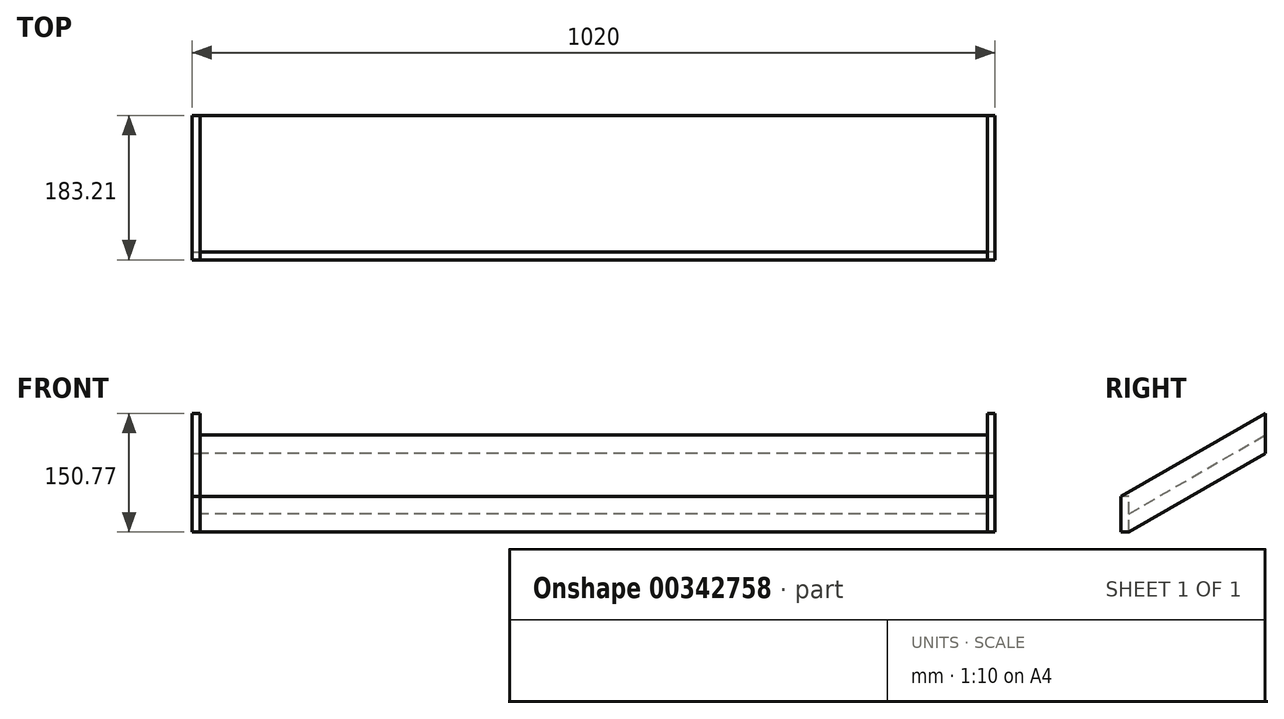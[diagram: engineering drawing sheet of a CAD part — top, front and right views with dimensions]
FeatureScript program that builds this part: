
annotation { "Feature Type Name" : "Feature", "Feature Type Description" : "" }
export const myFeature = defineFeature(function(context is Context, id is Id, definition is map)
    precondition{}
    {
        {
            var Q0;
            Q0=qCreatedBy(makeId("Right.planeOp"),FACE);
            var sketch = newSketch(context, id + "F0", { "sketchPlane" : qUnion([Q0])});
            skLineSegment(sketch, "E0", {"start": v(0, 100) * mm, "end": v(-173.2, 0) * mm});
            skLineSegment(sketch, "E1", {"start": v(-173.2, 0) * mm, "end": v(-173.2, 23.1) * mm});
            skLineSegment(sketch, "E2", {"start": v(-173.2, 23.1) * mm, "end": v(0, 123.1) * mm});
            skLineSegment(sketch, "E3", {"start": v(0, 123.1) * mm, "end": v(0, 100) * mm});
            skLineSegment(sketch, "E4", {"start": v(0, 0) * mm, "end": v(0, 143.65) * mm, "construction": true});
            skSolve(sketch);
        }
        {
            var Q0;
            Q0 = qSketchRegion(id + "F0", true);
            extrude(context, id + "F1", {"entities" : qUnion([Q0]), "endBound" : BoundingType.SYMMETRIC, "depth" : 1000 * mm});
        }
        {
            var Q0;
            Q0=makeQuery(id+"F1.opExtrude","CAP_FACE",FACE,{"disambiguationData":[OSD([sQuery(id+"F0.wireOp",EDGE,"E0"),sQuery(id+"F0.wireOp",EDGE,"E1"),sQuery(id+"F0.wireOp",EDGE,"E2"),sQuery(id+"F0.wireOp",EDGE,"E3")])],"isStart":true});
            var sketch = newSketch(context, id + "F2", { "sketchPlane" : qUnion([Q0])});
            skLineSegment(sketch, "E5.bottom", {"start": v(173.2, 0) * mm, "end": v(183.2, 0) * mm});
            skLineSegment(sketch, "E5.top", {"start": v(173.2, 45) * mm, "end": v(183.2, 45) * mm});
            skLineSegment(sketch, "E5.left", {"start": v(173.2, 0) * mm, "end": v(173.2, 45) * mm});
            skLineSegment(sketch, "E5.right", {"start": v(183.2, 0) * mm, "end": v(183.2, 45) * mm});
            skSolve(sketch);
        }
        {
            var Q0;
            Q0 = qSketchRegion(id + "F2", true);
            extrude(context, id + "F3", {"entities" : qUnion([Q0]), "oppositeDirection" : true, "depth" : 1000 * mm});
        }
        {
            var Q0;
            Q0=makeQuery(id+"F1.opExtrude","CAP_FACE",FACE,{"disambiguationData":[OSD([sQuery(id+"F0.wireOp",EDGE,"E0"),sQuery(id+"F0.wireOp",EDGE,"E1"),sQuery(id+"F0.wireOp",EDGE,"E2"),sQuery(id+"F0.wireOp",EDGE,"E3")])],"isStart":true});
            var sketch = newSketch(context, id + "F4", { "sketchPlane" : qUnion([Q0])});
            skLineSegment(sketch, "E6", {"start": v(0, 100) * mm, "end": v(173.2, 0) * mm});
            skLineSegment(sketch, "E7", {"start": v(173.2, 0) * mm, "end": v(183.2, 0) * mm});
            skLineSegment(sketch, "E8", {"start": v(183.2, 0) * mm, "end": v(183.2, 45) * mm});
            skLineSegment(sketch, "E9", {"start": v(183.2, 45) * mm, "end": v(0, 150.77) * mm});
            skLineSegment(sketch, "E10", {"start": v(0, 150.77) * mm, "end": v(0, 100) * mm});
            skSolve(sketch);
        }
        {
            var Q0;
            Q0 = qSketchRegion(id + "F4", true);
            extrude(context, id + "F5", {"entities" : qUnion([Q0]), "depth" : 10 * mm});
        }
        {
            var Q0;
            Q0=makeQuery(id+"F5.opExtrude","SWEPT_BODY",BODY,{"disambiguationData":[OSD([sQuery(id+"F4.wireOp",EDGE,"E6"),sQuery(id+"F4.wireOp",EDGE,"E7"),sQuery(id+"F4.wireOp",EDGE,"E8"),sQuery(id+"F4.wireOp",EDGE,"E9"),sQuery(id+"F4.wireOp",EDGE,"E10")])]});
            var Q1;
            Q1=qCreatedBy(makeId("Right.planeOp"),FACE);
            mirror(context, id + "F6", {"entities" : qUnion([Q0]), "mirrorPlane" : qUnion([Q1])});
        }
    });
